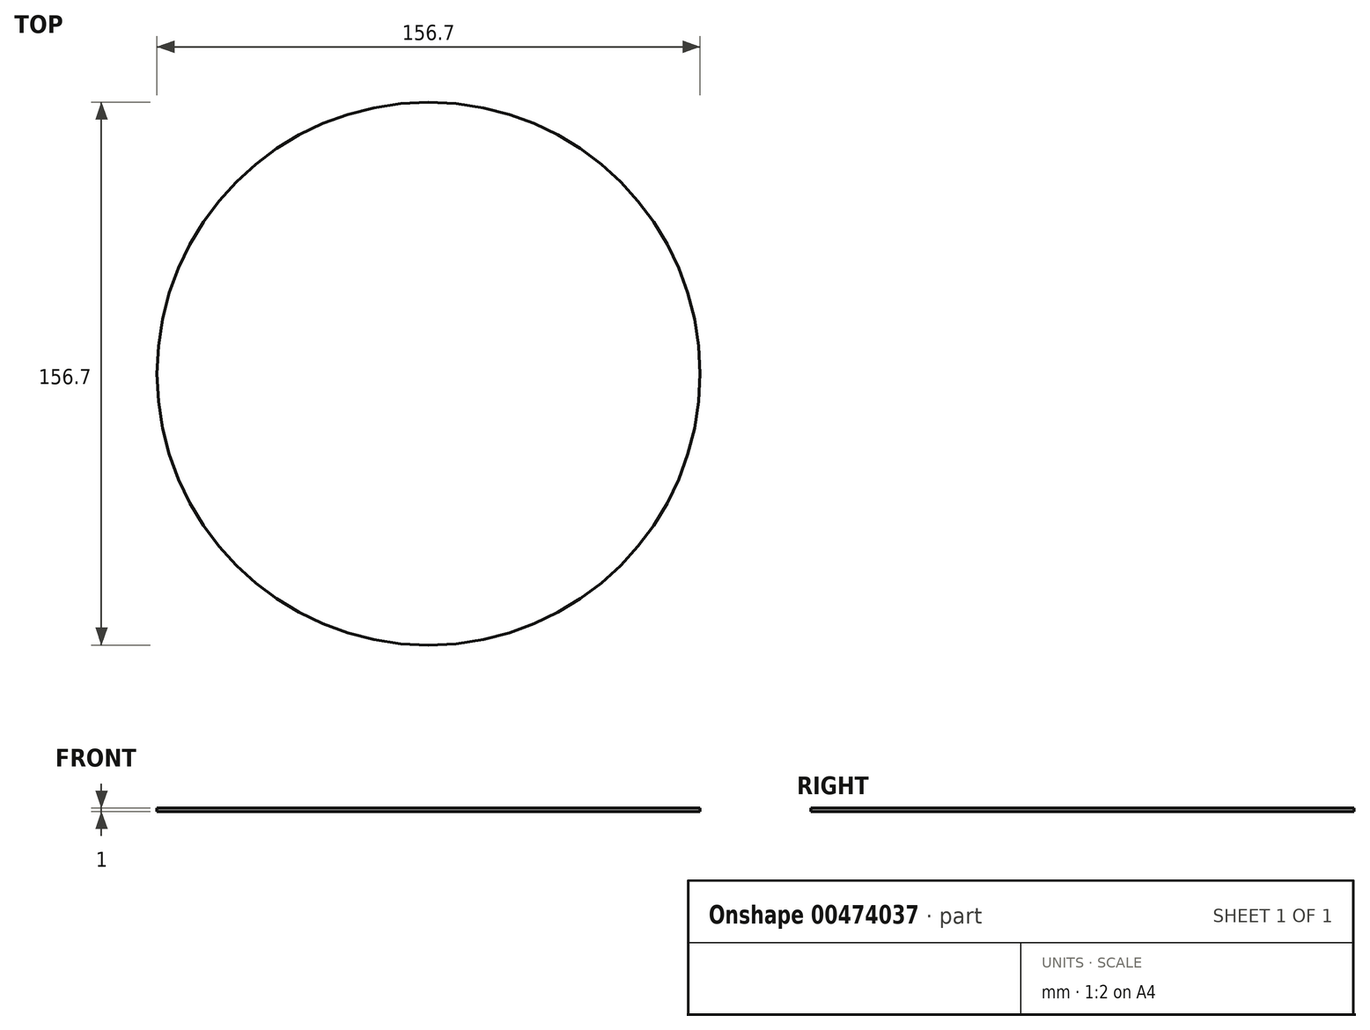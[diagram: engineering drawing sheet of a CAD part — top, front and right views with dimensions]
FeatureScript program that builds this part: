
annotation { "Feature Type Name" : "Feature", "Feature Type Description" : "" }
export const myFeature = defineFeature(function(context is Context, id is Id, definition is map)
    precondition{}
    {
        {
            var Q0;
            Q0=qCreatedBy(makeId("Top.planeOp"),FACE);
            var sketch = newSketch(context, id + "F0", { "sketchPlane" : qUnion([Q0])});
            skCircle(sketch, "E0", {"center": v(0, 0) * mm, "radius": 78.35 * mm});
            skSolve(sketch);
        }
        {
            var Q0;
            Q0 = qSketchRegion(id + "F0", true);
            extrude(context, id + "F1", {"entities" : qUnion([Q0]), "depth" : 1 * mm});
        }
    });
